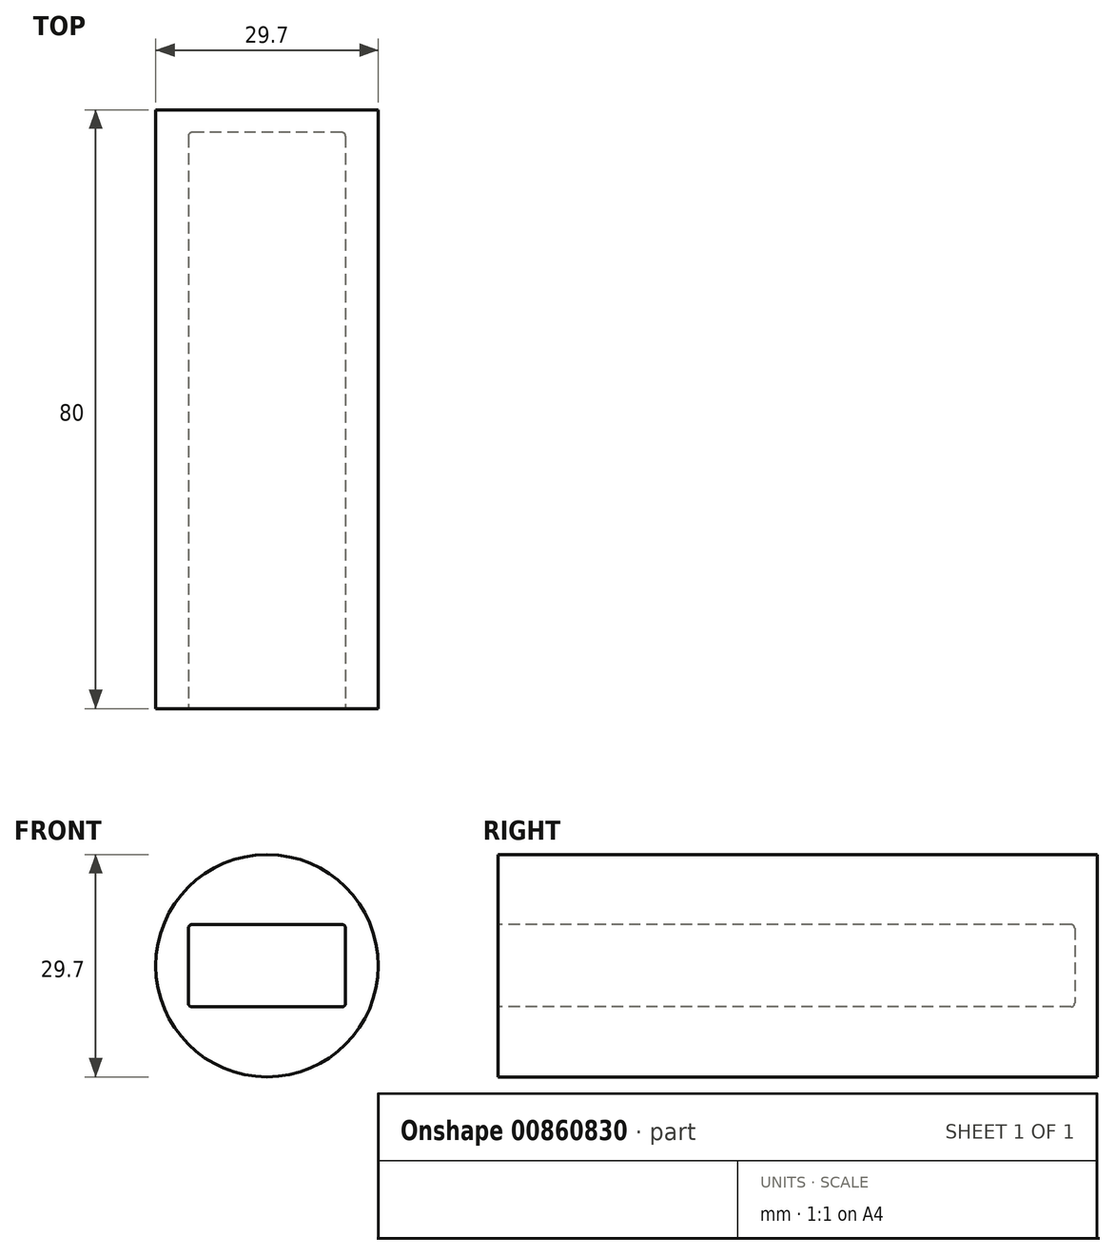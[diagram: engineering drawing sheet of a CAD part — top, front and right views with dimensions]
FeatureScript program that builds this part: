
annotation { "Feature Type Name" : "Feature", "Feature Type Description" : "" }
export const myFeature = defineFeature(function(context is Context, id is Id, definition is map)
    precondition{}
    {
        {
            assignVariable(context, id + "F0", {"name" : "hossz", "anyValue" : 76});
        }
        {
            assignVariable(context, id + "F1", {"name" : "letores", "anyValue" : 1});
        }
        {
            assignVariable(context, id + "F2", {"name" : "belso_r", "anyValue" : 0.5});
        }
        {
            var Q0;
            Q0=qCreatedBy(makeId("Front.planeOp"),FACE);
            var sketch = newSketch(context, id + "F3", { "sketchPlane" : qUnion([Q0])});
            skLineSegment(sketch, "E0.bottom", {"start": v(10.5, 5.5) * mm, "end": v(-10.5, 5.5) * mm});
            skLineSegment(sketch, "E0.top", {"start": v(10.5, -5.5) * mm, "end": v(-10.5, -5.5) * mm});
            skLineSegment(sketch, "E0.left", {"start": v(10.5, 5.5) * mm, "end": v(10.5, -5.5) * mm});
            skLineSegment(sketch, "E0.right", {"start": v(-10.5, 5.5) * mm, "end": v(-10.5, -5.5) * mm});
            skPoint(sketch, "E0.middle", {"position": v(0, 0) * mm});
            skCircle(sketch, "E1", {"center": v(0, 0) * mm, "radius": 14.85 * mm});
            skSolve(sketch);
        }
        {
            var Q0;
            Q0 = qSketchRegion(id + "F3", true);
            extrude(context, id + "F4", {"entities" : qUnion([Q0]), "oppositeDirection" : true, "depth" : (getVariable(context, 'hossz') + getVariable(context, 'letores')) * mm, "offsetDistance" : 25 * mm});
        }
        {
            var Q0;
            Q0=makeQuery(id+"F4.opExtrude","CAP_FACE",FACE,{"disambiguationData":[OSD([sQuery(id+"F3.wireOp",EDGE,"E0.bottom"),sQuery(id+"F3.wireOp",EDGE,"E0.top"),sQuery(id+"F3.wireOp",EDGE,"E0.left"),sQuery(id+"F3.wireOp",EDGE,"E0.right"),sQuery(id+"F3.wireOp",EDGE,"E1")])],"isStart":false});
            var sketch = newSketch(context, id + "F5", { "sketchPlane" : qUnion([Q0])});
            skCircle(sketch, "E2.0", {"center": v(0, 0) * mm, "radius": 14.85 * mm});
            skSolve(sketch);
        }
        {
            var Q0;
            Q0 = qSketchRegion(id + "F5", true);
            extrude(context, id + "F6", {"entities" : qUnion([Q0]), "operationType" : NewBodyOperationType.ADD, "depth" : 3 * mm, "offsetDistance" : 25 * mm});
        }
        {
            var Q0;
            Q0=makeQuery(id+"F6.opExtrude","CAP_FACE",FACE,{"disambiguationData":[OSD([sQuery(id+"F5.wireOp",EDGE,"E2.0")])],"isStart":true});
            var Q1;
            Q1=makeQuery(id+"F4.opExtrude","SWEPT_EDGE",EDGE,{"disambiguationData":[OSD([sQuery(id+"F3.wireOp",EDGE,"E0.top"),sQuery(id+"F3.wireOp",EDGE,"E0.right")])]});
            var Q2;
            Q2=makeQuery(id+"F4.opExtrude","SWEPT_EDGE",EDGE,{"disambiguationData":[OSD([sQuery(id+"F3.wireOp",EDGE,"E0.bottom"),sQuery(id+"F3.wireOp",EDGE,"E0.right")])]});
            var Q3;
            Q3=makeQuery(id+"F4.opExtrude","SWEPT_EDGE",EDGE,{"disambiguationData":[OSD([sQuery(id+"F3.wireOp",EDGE,"E0.bottom"),sQuery(id+"F3.wireOp",EDGE,"E0.left")])]});
            var Q4;
            Q4=makeQuery(id+"F4.opExtrude","SWEPT_EDGE",EDGE,{"disambiguationData":[OSD([sQuery(id+"F3.wireOp",EDGE,"E0.top"),sQuery(id+"F3.wireOp",EDGE,"E0.left")])]});
            fillet(context, id + "F7", {"entities" : qUnion([Q0, Q1, Q2, Q3, Q4]), "radius" : (getVariable(context, 'belso_r')) * mm, "tangentPropagation" : true, "allowEdgeOverflow" : false});
        }
    });
